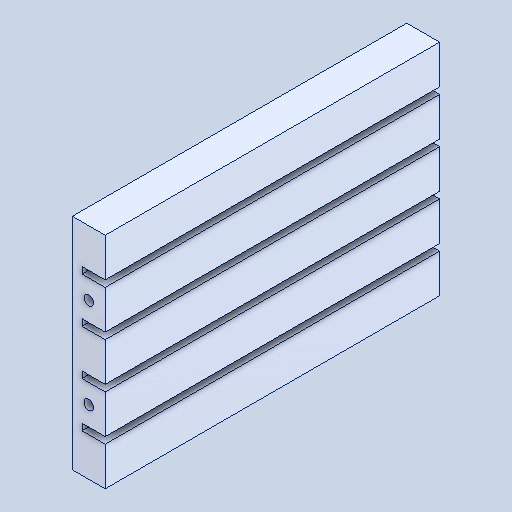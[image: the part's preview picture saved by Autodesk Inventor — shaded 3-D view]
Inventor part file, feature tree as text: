
AUTODESK INVENTOR PART (.ipt)
format: ipt  version: 2022 (Build 260153000, 153)  size: 131,072 bytes
history: mixed  units: in
note: dims shown in document units (in); Inventor stores cm internally (conversion verified against a paired STEP export)
features: mirror x1, imported_body x1
ambient origin geometry x8: Origin, YZ Plane, XZ Plane, XY Plane, X Axis, Y Axis, Z Axis, Center Point
bodies: Solid1 (imported_parasolid)
feature tree (2):
  mirror  "Mirror2"
  imported_body  NMx_Import_Brep_tag  [imported B-rep: ~38 faces, bbox_mm=[8.5, 56.8, 86.5]]
